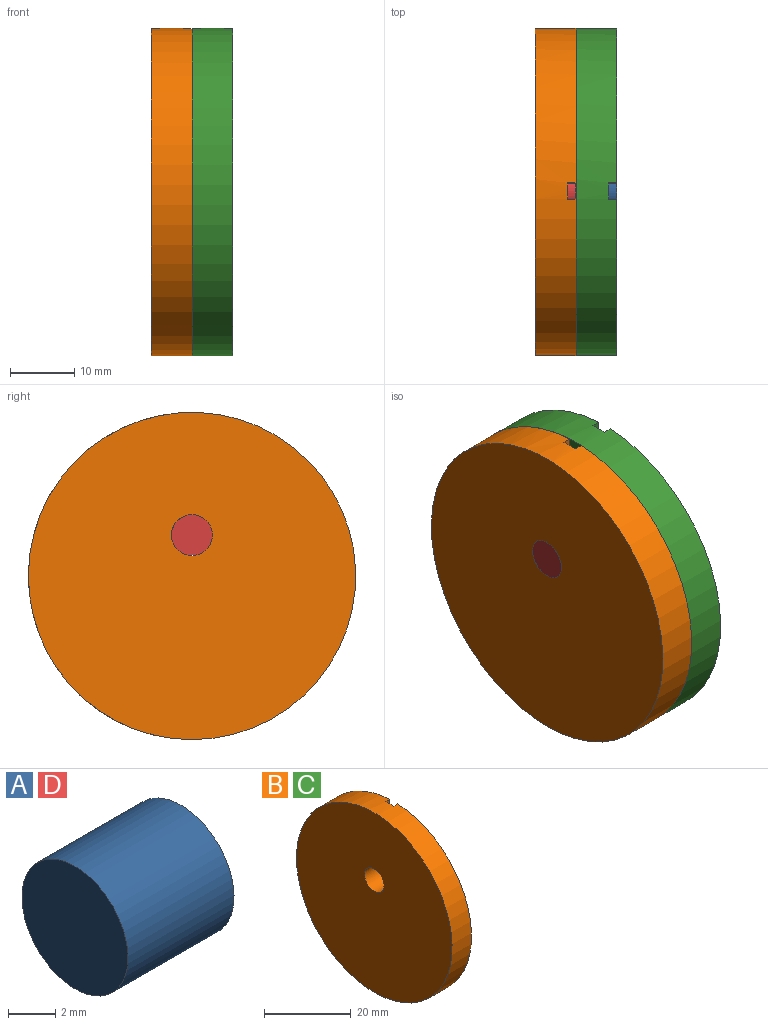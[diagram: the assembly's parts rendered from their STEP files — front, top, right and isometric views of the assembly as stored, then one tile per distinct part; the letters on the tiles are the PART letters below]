
ASSEMBLY  parts=4 mates=4
PART A: 3 faces, bbox 6.4x6.4x6.4 mm
  f0: cylinder r=3.17mm len=6.35mm, axis (-1,0,0), area 126.7mm2, adj f1,f2
  f1: plane 6.35x6.35mm, normal (1,0,0), area 31.7mm2, adj f0
  f2: plane 6.35x6.35mm, normal (-1,0,0), area 31.7mm2, adj f0
PART B: 11 faces, bbox 6.4x50.8x50.8 mm
  f0: cylinder r=25.4mm len=50.8mm, axis (-1,0,0), area 1010.2mm2, adj f1,f2,f8,f9,f10
  f1: plane 50.8x50.77mm, normal (1,0,0), area 1946.4mm2, adj f0,f3,f5,f6,f7,f8,f9
  f2: plane 50.8x50.8mm, normal (-1,0,0), area 1995.2mm2, adj f0,f3
  f3: cylinder r=3.17mm len=6.35mm, axis (1,0,0), area 120mm2, adj f1,f2,f4,f5,f6,f8,f9,f10
  f4: plane 3.44x2.54mm, normal (1,0,0), area 8.3mm2, adj f3,f5,f6,f7
  f5: plane 3.44x1.27mm, normal (0,-1,0), area 4.4mm2, adj f1,f3,f4,f7
  f6: plane 3.44x1.27mm, normal (0,1,0), area 4.4mm2, adj f1,f3,f4,f7
  f7: plane 2.54x1.27mm, normal (0,0,1), area 3.2mm2, adj f1,f4,f5,f6
  f8: plane 16.11x1.27mm, normal (0,1,0), area 20.5mm2, adj f0,f1,f3,f10
  f9: plane 16.11x1.27mm, normal (0,-1,0), area 20.5mm2, adj f0,f1,f3,f10
  f10: plane 16.14x2.54mm, normal (1,0,0), area 40.5mm2, adj f0,f3,f8,f9
PART C: same geometry as B
PART D: same geometry as A
PLACE A t=(-6.35,-52.05,-5.69)mm
PLACE B rot(axis=(-1,0,0),0.3deg) t=(-12.7,-0.03,-6.35)mm
PLACE C rot(axis=(-1,0,0),0.3deg) t=(-6.35,-0.03,-6.35)mm
PLACE D t=(-12.7,-52.05,-5.69)mm
MATE revolute B.f3 <-> D.f0  axis (1,0,0) through (-9.52,0,0)mm
MATE revolute C.f3 <-> A.f0  axis (1,0,0) through (-3.17,0,0)mm
MATE planar B.f1 <-> C.f2  axis (1,0,0) through (-6.35,-0.03,-6.82)mm
MATE cylindrical B.f3 <-> A.f0  axis (1,0,0) through (-6.35,0,0)mm
